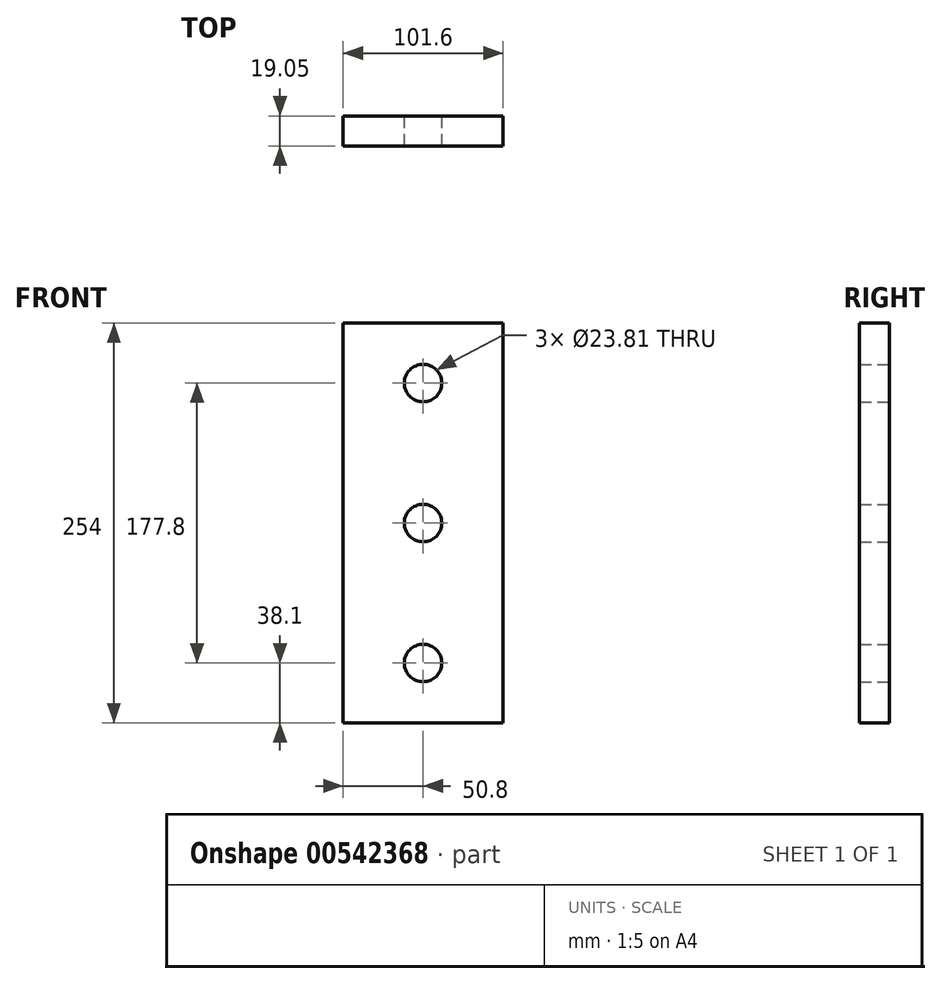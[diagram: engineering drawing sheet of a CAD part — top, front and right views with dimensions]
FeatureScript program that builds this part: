
annotation { "Feature Type Name" : "Feature", "Feature Type Description" : "" }
export const myFeature = defineFeature(function(context is Context, id is Id, definition is map)
    precondition{}
    {
        {
            var Q0;
            Q0=qCreatedBy(makeId("Front.planeOp"),FACE);
            var sketch = newSketch(context, id + "F0", { "sketchPlane" : qUnion([Q0])});
            skLineSegment(sketch, "E0.bottom", {"start": v(50.8, -127) * mm, "end": v(-50.8, -127) * mm});
            skLineSegment(sketch, "E0.top", {"start": v(50.8, 127) * mm, "end": v(-50.8, 127) * mm});
            skLineSegment(sketch, "E0.left", {"start": v(50.8, -127) * mm, "end": v(50.8, 127) * mm});
            skLineSegment(sketch, "E0.right", {"start": v(-50.8, -127) * mm, "end": v(-50.8, 127) * mm});
            skPoint(sketch, "E0.middle", {"position": v(0, 0) * mm});
            skCircle(sketch, "E1", {"center": v(0, 0) * mm, "radius": 11.9 * mm});
            skCircle(sketch, "E2", {"center": v(0, 88.9) * mm, "radius": 11.9 * mm});
            skCircle(sketch, "E3", {"center": v(0, -88.9) * mm, "radius": 11.9 * mm});
            skSolve(sketch);
        }
        {
            var Q0;
            Q0=makeQuery(id+"F0.imprint","IMPRINT",FACE,{"disambiguationData":[TD([[makeQuery(id+"F0.imprint","IMPRINT",EDGE,{"derivedFrom":sQuery(id+"F0.wireOp",EDGE,"E0.bottom")}),-1.0]])]});
            extrude(context, id + "F1", {"entities" : qUnion([Q0]), "depth" : 19.05 * mm, "offsetDistance" : 25.4 * mm});
        }
    });
